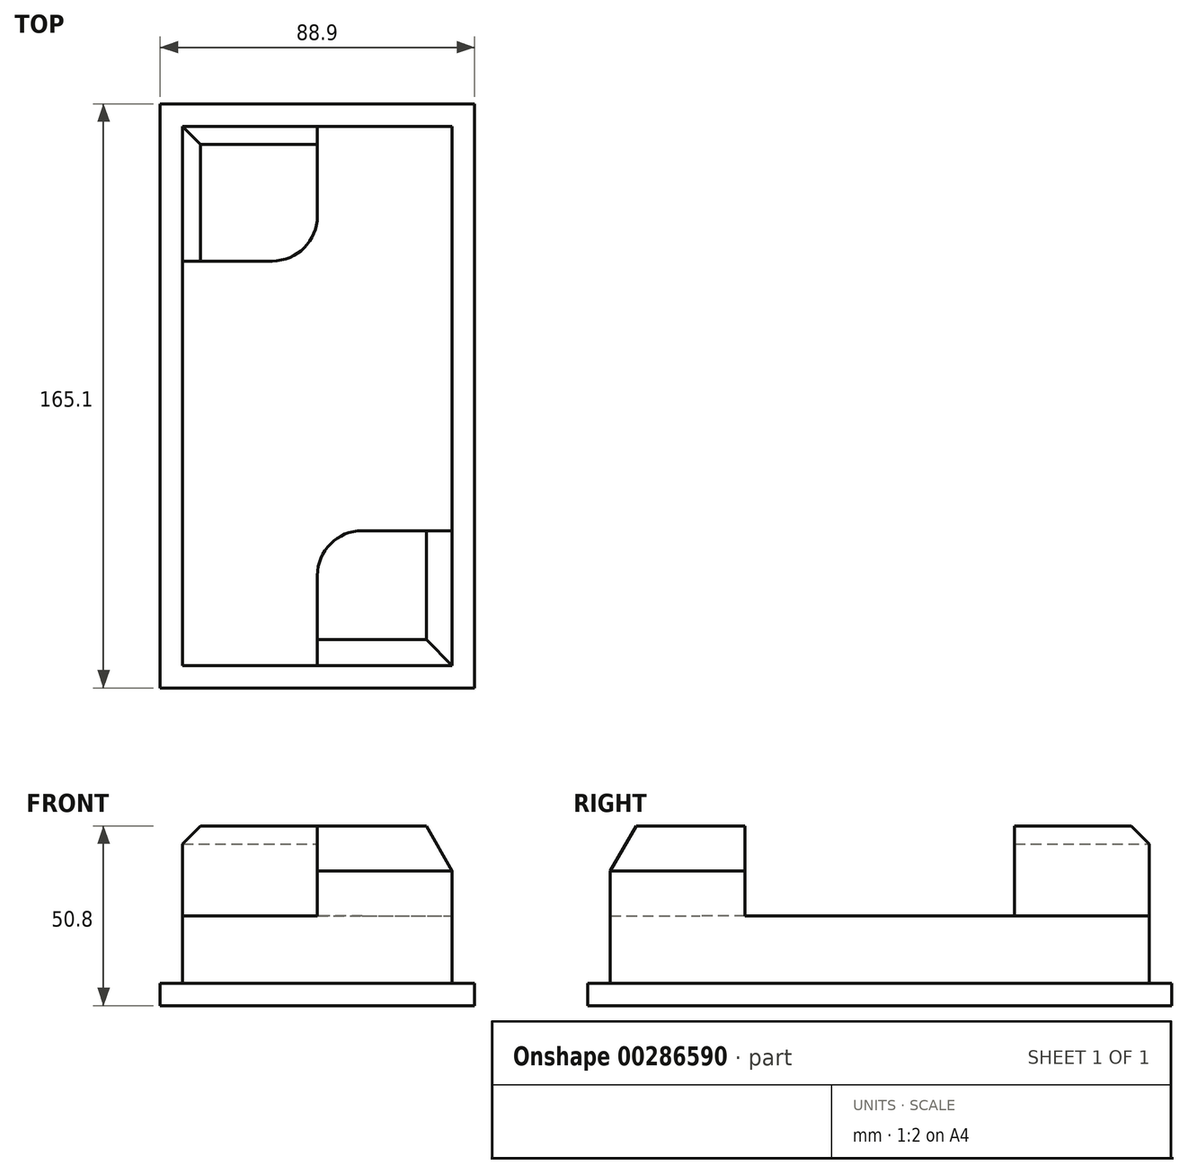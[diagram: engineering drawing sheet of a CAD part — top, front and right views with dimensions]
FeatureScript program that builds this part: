
annotation { "Feature Type Name" : "Feature", "Feature Type Description" : "" }
export const myFeature = defineFeature(function(context is Context, id is Id, definition is map)
    precondition{}
    {
        {
            var Q0;
            Q0=qCreatedBy(makeId("Top.planeOp"),FACE);
            var sketch = newSketch(context, id + "F0", { "sketchPlane" : qUnion([Q0])});
            skLineSegment(sketch, "E0.bottom", {"start": v(-41.13, -88.36) * mm, "end": v(47.77, -88.36) * mm});
            skLineSegment(sketch, "E0.top", {"start": v(-41.13, 76.74) * mm, "end": v(47.77, 76.74) * mm});
            skLineSegment(sketch, "E0.left", {"start": v(-41.13, -88.36) * mm, "end": v(-41.13, 76.74) * mm});
            skLineSegment(sketch, "E0.right", {"start": v(47.77, -88.36) * mm, "end": v(47.77, 76.74) * mm});
            skLineSegment(sketch, "E1.0", {"start": v(-34.78, 70.4) * mm, "end": v(41.42, 70.4) * mm});
            skLineSegment(sketch, "E1.1", {"start": v(-34.78, -82) * mm, "end": v(-34.78, 70.4) * mm});
            skLineSegment(sketch, "E1.2", {"start": v(-34.78, -82) * mm, "end": v(41.42, -82) * mm});
            skLineSegment(sketch, "E1.3", {"start": v(41.42, -82) * mm, "end": v(41.42, 70.4) * mm});
            skLineSegment(sketch, "E2", {"start": v(3.32, 70.4) * mm, "end": v(3.32, 45) * mm});
            skLineSegment(sketch, "E3", {"start": v(-9.38, 32.3) * mm, "end": v(-34.78, 32.3) * mm});
            skLineSegment(sketch, "E4", {"start": v(3.32, -82) * mm, "end": v(3.32, -56.6) * mm});
            skLineSegment(sketch, "E5", {"start": v(16.02, -43.9) * mm, "end": v(41.42, -43.9) * mm});
            skPoint(sketch, "E6.visualSharp", {"position": v(3.32, 32.3) * mm});
            skArc(sketch, "E6.filletArc", {"start": v(-9.38, 32.3) * mm, "mid": v(-0.4, 36) * mm, "end": v(3.32, 45) * mm});
            skPoint(sketch, "E7.visualSharp", {"position": v(3.32, -43.9) * mm});
            skArc(sketch, "E7.filletArc", {"start": v(16.02, -43.9) * mm, "mid": v(7.04, -47.63) * mm, "end": v(3.32, -56.6) * mm});
            skLineSegment(sketch, "E8", {"start": v(41.42, 70.4) * mm, "end": v(47.77, 70.4) * mm, "construction": true});
            skSolve(sketch);
        }
        {
            var Q0;
            Q0=makeQuery(id+"F0.imprint","IMPRINT",FACE,{"disambiguationData":[TD([[makeQuery(id+"F0.imprint","IMPRINT",EDGE,{"derivedFrom":sQuery(id+"F0.wireOp",EDGE,"E0.bottom")}),1.0]])]});
            extrude(context, id + "F1", {"entities" : qUnion([Q0]), "depth" : 6.35 * mm});
        }
        {
            var Q0;
            {var subQ9=sQuery(id+"F0.wireOp",EDGE,"E2");Q0=makeQuery(id+"F0.imprint","IMPRINT",FACE,{"disambiguationData":[TD([[makeQuery(id+"F0.imprint","IMPRINT",EDGE,{"derivedFrom":subQ9}),1.0]])]});}
            extrude(context, id + "F2", {"entities" : qUnion([Q0]), "operationType" : NewBodyOperationType.ADD, "depth" : 25.4 * mm});
        }
        {
            var Q0;
            {var subQ1=sQuery(id+"F0.wireOp",EDGE,"E2");Q0=makeQuery(id+"F0.imprint","IMPRINT",FACE,{"disambiguationData":[TD([[makeQuery(id+"F0.imprint","IMPRINT",EDGE,{"derivedFrom":subQ1}),-1.0]])]});}
            var Q1;
            {var subQ4=sQuery(id+"F0.wireOp",EDGE,"E4");Q1=makeQuery(id+"F0.imprint","IMPRINT",FACE,{"disambiguationData":[TD([[makeQuery(id+"F0.imprint","IMPRINT",EDGE,{"derivedFrom":subQ4}),-1.0]])]});}
            extrude(context, id + "F3", {"entities" : qUnion([Q0, Q1]), "operationType" : NewBodyOperationType.ADD, "depth" : 50.8 * mm});
        }
        {
            var Q0;
            Q0=makeQuery(id+"F3.opExtrude","CAP_EDGE",EDGE,{"disambiguationData":[OSD([sQuery(id+"F0.wireOp",EDGE,"E1.2")])],"isStart":false});
            var Q1;
            Q1=makeQuery(id+"F3.opExtrude","CAP_EDGE",EDGE,{"disambiguationData":[OSD([sQuery(id+"F0.wireOp",EDGE,"E1.3")])],"isStart":false});
            chamfer(context, id + "F4", {"entities" : qUnion([Q0, Q1]), "chamferType" : ChamferType.OFFSET_ANGLE, "width" : 12.7 * mm, "oppositeDirection" : true, "angle" : 30 * degree, "tangentPropagation" : true});
        }
        {
            var Q0;
            Q0=makeQuery(id+"F3.opExtrude","CAP_EDGE",EDGE,{"disambiguationData":[OSD([sQuery(id+"F0.wireOp",EDGE,"E1.0")])],"isStart":false});
            var Q1;
            Q1=makeQuery(id+"F3.opExtrude","CAP_EDGE",EDGE,{"disambiguationData":[OSD([sQuery(id+"F0.wireOp",EDGE,"E1.1")])],"isStart":false});
            chamfer(context, id + "F5", {"entities" : qUnion([Q0, Q1]), "width" : 5.08 * mm, "tangentPropagation" : true});
        }
    });
